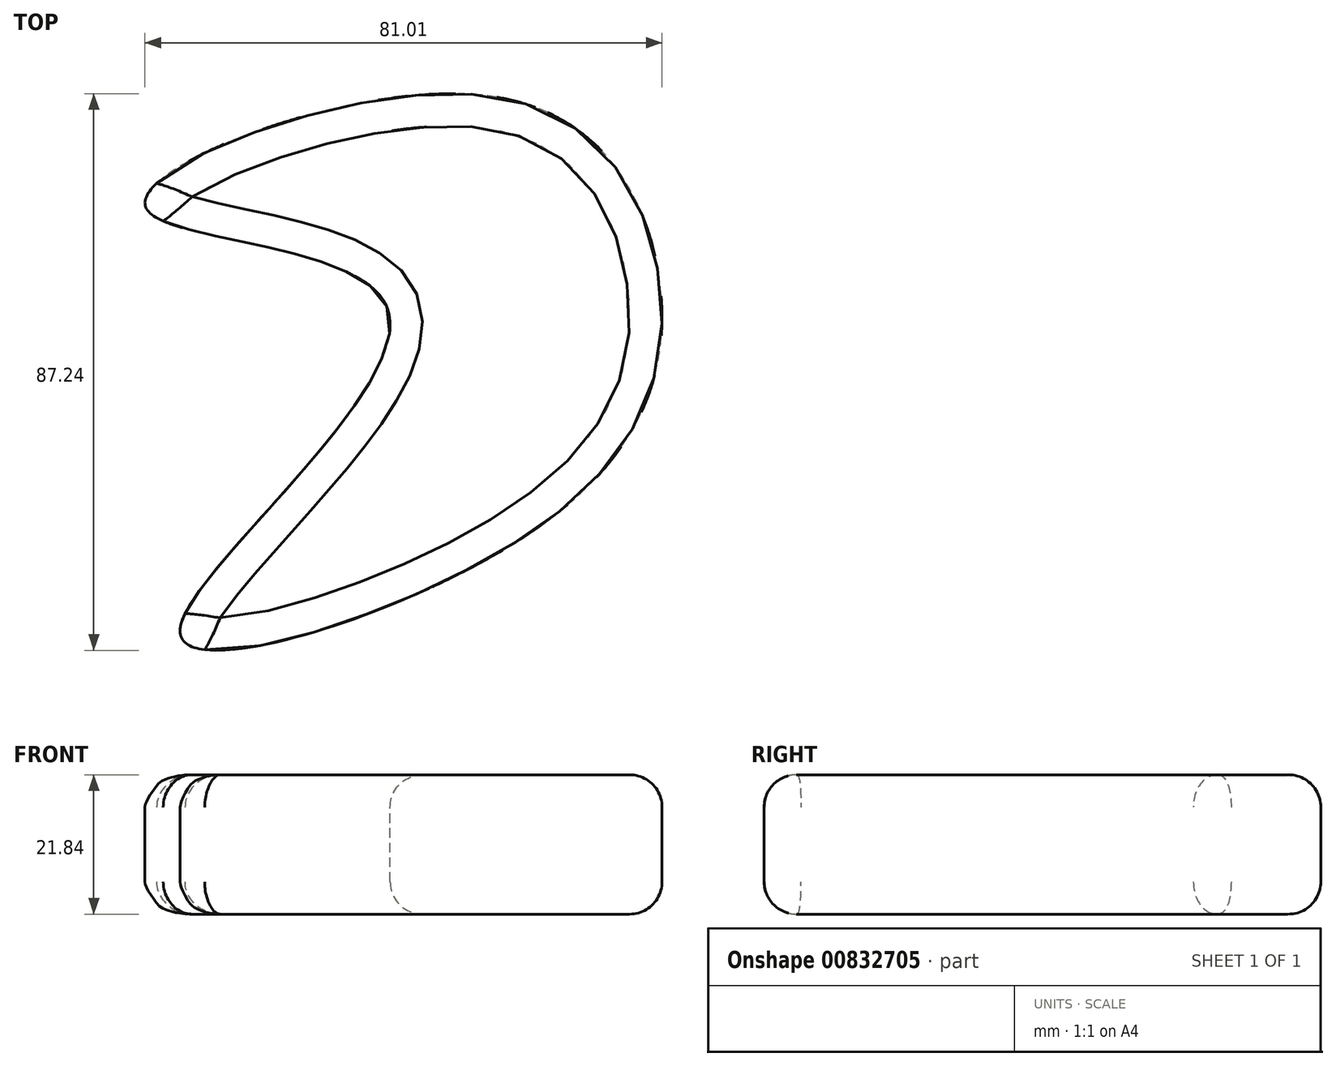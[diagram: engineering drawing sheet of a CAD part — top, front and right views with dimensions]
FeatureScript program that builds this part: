
annotation { "Feature Type Name" : "Feature", "Feature Type Description" : "" }
export const myFeature = defineFeature(function(context is Context, id is Id, definition is map)
    precondition{}
    {
        {
            var Q0;
            Q0=qCreatedBy(makeId("Top.planeOp"),FACE);
            var sketch = newSketch(context, id + "F0", { "sketchPlane" : qUnion([Q0])});
            skFitSpline(sketch, "E0", {"points": [v(0, 0) * mm, v(-32.61, -50.32) * mm, v(22.86, -34.45) * mm, v(42.52, 4.6) * mm, v(15.19, 33.66) * mm, v(-37.87, 15.9) * mm, v(0, 0) * mm]});
            skSolve(sketch);
        }
        {
            var Q0;
            Q0=makeQuery(id+"F0.imprint","IMPRINT",FACE,{"disambiguationData":[TD([[makeQuery(id+"F0.imprint","IMPRINT",EDGE,{"derivedFrom":sQuery(id+"F0.wireOp",EDGE,"E0")}),1.0]])]});
            extrude(context, id + "F1", {"entities" : qUnion([Q0]), "depth" : 21.84 * mm, "offsetDistance" : 25.4 * mm});
        }
        {
            var Q0;
            Q0=makeQuery(id+"F1.opExtrude","CAP_FACE",FACE,{"disambiguationData":[OSD([sQuery(id+"F0.wireOp",EDGE,"E0")])],"isStart":false});
            fillet(context, id + "F2", {"entities" : qUnion([Q0]), "radius" : 5.08 * mm, "tangentPropagation" : true, "allowEdgeOverflow" : false});
        }
        {
            var Q0;
            Q0=makeQuery(id+"F1.opExtrude","CAP_FACE",FACE,{"disambiguationData":[OSD([sQuery(id+"F0.wireOp",EDGE,"E0")])],"isStart":true});
            fillet(context, id + "F3", {"entities" : qUnion([Q0]), "radius" : 5.08 * mm, "tangentPropagation" : true, "allowEdgeOverflow" : false});
        }
    });
